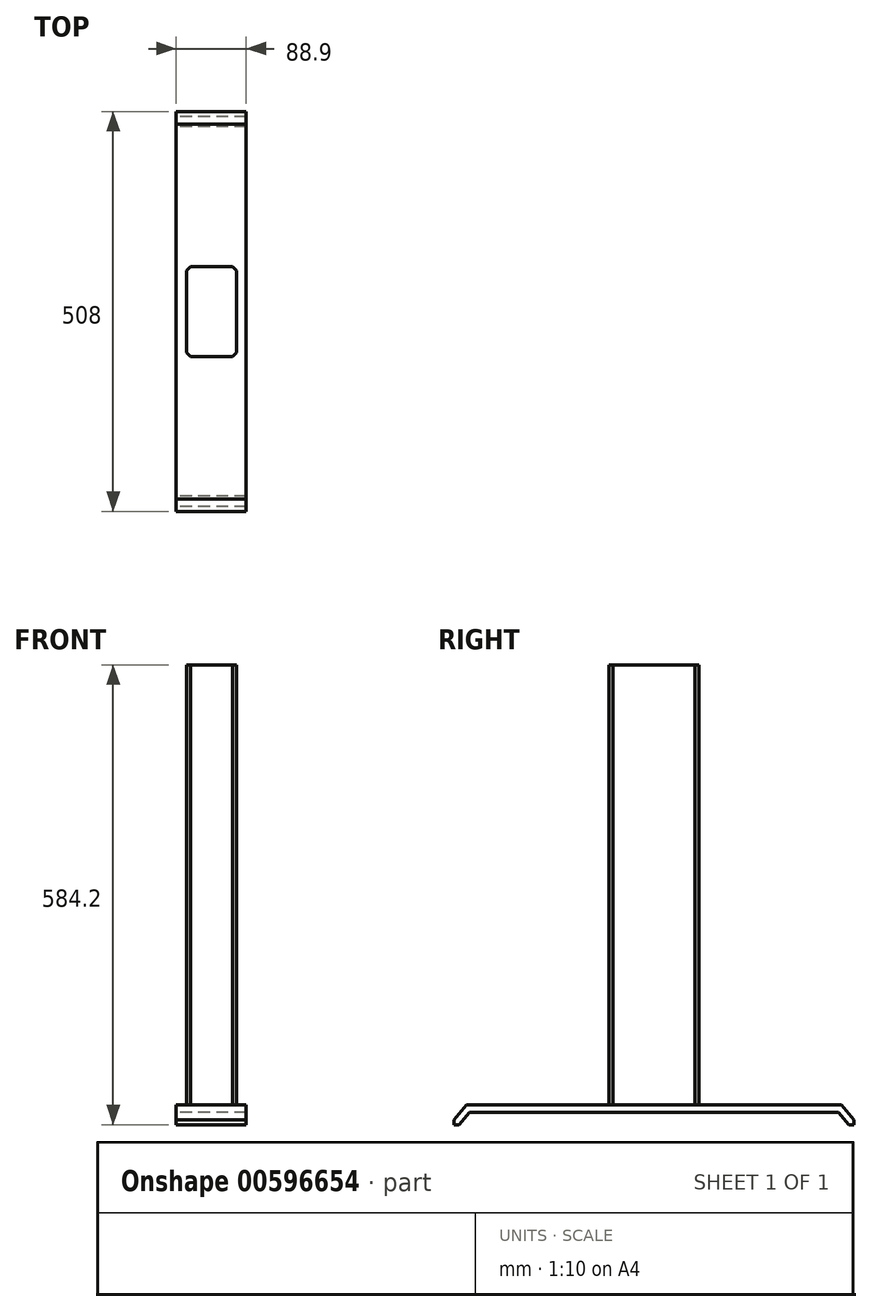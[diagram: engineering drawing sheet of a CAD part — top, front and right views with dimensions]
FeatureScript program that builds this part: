
annotation { "Feature Type Name" : "Feature", "Feature Type Description" : "" }
export const myFeature = defineFeature(function(context is Context, id is Id, definition is map)
    precondition{}
    {
        {
            var Q0;
            Q0=qCreatedBy(makeId("Top.planeOp"),FACE);
            var sketch = newSketch(context, id + "F0", { "sketchPlane" : qUnion([Q0])});
            skLineSegment(sketch, "E0.bottom", {"start": v(-31.75, 57.15) * mm, "end": v(31.75, 57.15) * mm});
            skLineSegment(sketch, "E0.top", {"start": v(-31.75, -57.15) * mm, "end": v(31.75, -57.15) * mm});
            skLineSegment(sketch, "E0.left", {"start": v(-31.75, 57.15) * mm, "end": v(-31.75, -57.15) * mm});
            skLineSegment(sketch, "E0.right", {"start": v(31.75, 57.15) * mm, "end": v(31.75, -57.15) * mm});
            skPoint(sketch, "E0.middle", {"position": v(0, 0) * mm});
            skSolve(sketch);
        }
        {
            var Q0;
            Q0=makeQuery(id+"F0.imprint","IMPRINT",FACE,{"disambiguationData":[TD([[makeQuery(id+"F0.imprint","IMPRINT",EDGE,{"derivedFrom":sQuery(id+"F0.wireOp",EDGE,"E0.bottom")}),-1.0]])]});
            extrude(context, id + "F1", {"entities" : qUnion([Q0]), "depth" : 558.8 * mm, "offsetDistance" : 25.4 * mm});
        }
        {
            var Q0;
            Q0=makeQuery(id+"F1.opExtrude","SWEPT_EDGE",EDGE,{"disambiguationData":[OSD([sQuery(id+"F0.wireOp",EDGE,"E0.bottom"),sQuery(id+"F0.wireOp",EDGE,"E0.right")])]});
            var Q1;
            Q1=makeQuery(id+"F1.opExtrude","SWEPT_EDGE",EDGE,{"disambiguationData":[OSD([sQuery(id+"F0.wireOp",EDGE,"E0.bottom"),sQuery(id+"F0.wireOp",EDGE,"E0.left")])]});
            var Q2;
            Q2=makeQuery(id+"F1.opExtrude","SWEPT_EDGE",EDGE,{"disambiguationData":[OSD([sQuery(id+"F0.wireOp",EDGE,"E0.top"),sQuery(id+"F0.wireOp",EDGE,"E0.left")])]});
            var Q3;
            Q3=makeQuery(id+"F1.opExtrude","SWEPT_EDGE",EDGE,{"disambiguationData":[OSD([sQuery(id+"F0.wireOp",EDGE,"E0.top"),sQuery(id+"F0.wireOp",EDGE,"E0.right")])]});
            chamfer(context, id + "F2", {"entities" : qUnion([Q0, Q1, Q2, Q3]), "width" : 5.08 * mm, "tangentPropagation" : true});
        }
        {
            var Q0;
            Q0=makeQuery(id+"F1.opExtrude","CAP_FACE",FACE,{"disambiguationData":[OSD([sQuery(id+"F0.wireOp",EDGE,"E0.bottom"),sQuery(id+"F0.wireOp",EDGE,"E0.top"),sQuery(id+"F0.wireOp",EDGE,"E0.left"),sQuery(id+"F0.wireOp",EDGE,"E0.right")])],"isStart":true});
            var sketch = newSketch(context, id + "F3", { "sketchPlane" : qUnion([Q0])});
            skLineSegment(sketch, "E1.bottom", {"start": v(31.75, 254) * mm, "end": v(-31.75, 254) * mm});
            skLineSegment(sketch, "E1.top", {"start": v(31.75, -254) * mm, "end": v(-31.75, -254) * mm});
            skLineSegment(sketch, "E1.left", {"start": v(31.75, 254) * mm, "end": v(31.75, -254) * mm});
            skLineSegment(sketch, "E1.right", {"start": v(-31.75, 254) * mm, "end": v(-31.75, -254) * mm});
            skPoint(sketch, "E1.middle", {"position": v(0, 0) * mm});
            skSolve(sketch);
        }
        {
            var Q0;
            {var subQ6=sQuery(id+"F3.wireOp",EDGE,"E1.bottom");Q0=makeQuery(id+"F3.imprint","IMPRINT",FACE,{"disambiguationData":[TD([[makeQuery(id+"F3.imprint","IMPRINT",EDGE,{"derivedFrom":subQ6}),1.0]])]});}
            var Q1;
            {var subQ3=sQuery(id+"F0.wireOp",EDGE,"E0.bottom");Q1=makeQuery(id+"F3.imprint","IMPRINT",FACE,{"disambiguationData":[TD([[makeQuery(id+"F3.imprint","IMPRINT",EDGE,{"derivedFrom":makeQuery(id+"F1.opExtrude","CAP_EDGE",EDGE,{"disambiguationData":[OSD([subQ3])],"isStart":true})}),1.0]])]});}
            var Q2;
            {var subQ6=sQuery(id+"F3.wireOp",EDGE,"E1.top");Q2=makeQuery(id+"F3.imprint","IMPRINT",FACE,{"disambiguationData":[TD([[makeQuery(id+"F3.imprint","IMPRINT",EDGE,{"derivedFrom":subQ6}),-1.0]])]});}
            extrude(context, id + "F4", {"entities" : qUnion([Q0, Q1, Q2]), "operationType" : NewBodyOperationType.ADD, "depth" : 25.4 * mm, "offsetDistance" : 25.4 * mm});
        }
        {
            var Q0;
            Q0=makeQuery(id+"F4.opExtrude","SWEPT_FACE",FACE,{"disambiguationData":[OSD([sQuery(id+"F3.wireOp",EDGE,"E1.right")])]});
            var sketch = newSketch(context, id + "F5", { "sketchPlane" : qUnion([Q0])});
            skLineSegment(sketch, "E2", {"start": v(254, -25.4) * mm, "end": v(254, -19.05) * mm});
            skLineSegment(sketch, "E3", {"start": v(254, 0) * mm, "end": v(238.12, 0) * mm});
            skLineSegment(sketch, "E4", {"start": v(254, -19.05) * mm, "end": v(238.12, 0) * mm});
            skLineSegment(sketch, "E5", {"start": v(254, -25.4) * mm, "end": v(247.65, -25.4) * mm});
            skLineSegment(sketch, "E6", {"start": v(247.65, -25.4) * mm, "end": v(226.48, 0) * mm});
            skLineSegment(sketch, "E7", {"start": v(238.12, 0) * mm, "end": v(238.12, -9.53) * mm});
            skLineSegment(sketch, "E8", {"start": v(238.12, -9.53) * mm, "end": v(234.42, -9.53) * mm});
            skLineSegment(sketch, "E9", {"start": v(-254, -25.4) * mm, "end": v(-247.65, -25.4) * mm});
            skLineSegment(sketch, "E10", {"start": v(-254, -25.4) * mm, "end": v(-254, -19.05) * mm});
            skLineSegment(sketch, "E11", {"start": v(-254, 0) * mm, "end": v(-238.12, 0) * mm});
            skLineSegment(sketch, "E12", {"start": v(-238.12, 0) * mm, "end": v(-254, -19.05) * mm});
            skLineSegment(sketch, "E13", {"start": v(-247.65, -25.4) * mm, "end": v(-226.48, 0) * mm});
            skLineSegment(sketch, "E14", {"start": v(-238.12, 0) * mm, "end": v(-238.12, -9.53) * mm});
            skLineSegment(sketch, "E15", {"start": v(-238.12, -9.52) * mm, "end": v(-234.42, -9.52) * mm});
            skLineSegment(sketch, "E16", {"start": v(234.42, -9.53) * mm, "end": v(-234.42, -9.53) * mm});
            skSolve(sketch);
        }
        {
            var Q0;
            {var subQ0=sQuery(id+"F5.wireOp",EDGE,"E3");Q0=makeQuery(id+"F5.imprint","IMPRINT",FACE,{"disambiguationData":[TD([[makeQuery(id+"F5.imprint","IMPRINT",EDGE,{"derivedFrom":subQ0}),1.0]])]});}
            var Q1;
            {var subQ3=sQuery(id+"F5.wireOp",EDGE,"E16");Q1=makeQuery(id+"F5.imprint","IMPRINT",FACE,{"disambiguationData":[TD([[makeQuery(id+"F5.imprint","IMPRINT",EDGE,{"derivedFrom":subQ3}),1.0]])]});}
            var Q2;
            {var subQ0=sQuery(id+"F5.wireOp",EDGE,"E11");Q2=makeQuery(id+"F5.imprint","IMPRINT",FACE,{"disambiguationData":[TD([[makeQuery(id+"F5.imprint","IMPRINT",EDGE,{"derivedFrom":subQ0}),1.0]])]});}
            extrude(context, id + "F6", {"entities" : qUnion([Q0, Q1, Q2]), "operationType" : NewBodyOperationType.REMOVE, "oppositeDirection" : true, "depth" : 76.2 * mm, "offsetDistance" : 25.4 * mm});
        }
        {
            var Q0;
            Q0=makeQuery(id+"F4.boolean.opBoolean","MERGE",FACE,{"derivedFrom":[makeQuery(id+"F1.opExtrude","SWEPT_FACE",FACE,{"disambiguationData":[OSD([sQuery(id+"F0.wireOp",EDGE,"E0.right")])]}),makeQuery(id+"F4.opExtrude","SWEPT_FACE",FACE,{"disambiguationData":[OSD([sQuery(id+"F3.wireOp",EDGE,"E1.left")])]})]});
            var sketch = newSketch(context, id + "F7", { "sketchPlane" : qUnion([Q0])});
            skLineSegment(sketch, "E17", {"start": v(52.07, 0) * mm, "end": v(-52.07, 0) * mm});
            skSolve(sketch);
        }
        {
            var Q0;
            Q0=makeQuery(id+"F7.imprint","IMPRINT",FACE,{"disambiguationData":[TD([[makeQuery(id+"F7.imprint","IMPRINT",EDGE,{"derivedFrom":sQuery(id+"F7.wireOp",EDGE,"E17")}),1.0]])]});
            extrude(context, id + "F8", {"entities" : qUnion([Q0]), "operationType" : NewBodyOperationType.ADD, "depth" : 12.7 * mm, "offsetDistance" : 25.4 * mm});
        }
        {
            var Q0;
            Q0=makeQuery(id+"F4.boolean.opBoolean","MERGE",FACE,{"derivedFrom":[makeQuery(id+"F1.opExtrude","SWEPT_FACE",FACE,{"disambiguationData":[OSD([sQuery(id+"F0.wireOp",EDGE,"E0.left")])]}),makeQuery(id+"F4.opExtrude","SWEPT_FACE",FACE,{"disambiguationData":[OSD([sQuery(id+"F3.wireOp",EDGE,"E1.right")])]})]});
            var sketch = newSketch(context, id + "F9", { "sketchPlane" : qUnion([Q0])});
            skLineSegment(sketch, "E18", {"start": v(52.07, 0) * mm, "end": v(-52.07, 0) * mm});
            skSolve(sketch);
        }
        {
            var Q0;
            Q0=makeQuery(id+"F9.imprint","IMPRINT",FACE,{"disambiguationData":[TD([[makeQuery(id+"F9.imprint","IMPRINT",EDGE,{"derivedFrom":sQuery(id+"F9.wireOp",EDGE,"E18")}),1.0]])]});
            extrude(context, id + "F10", {"entities" : qUnion([Q0]), "operationType" : NewBodyOperationType.ADD, "depth" : 12.7 * mm, "offsetDistance" : 25.4 * mm});
        }
    });
